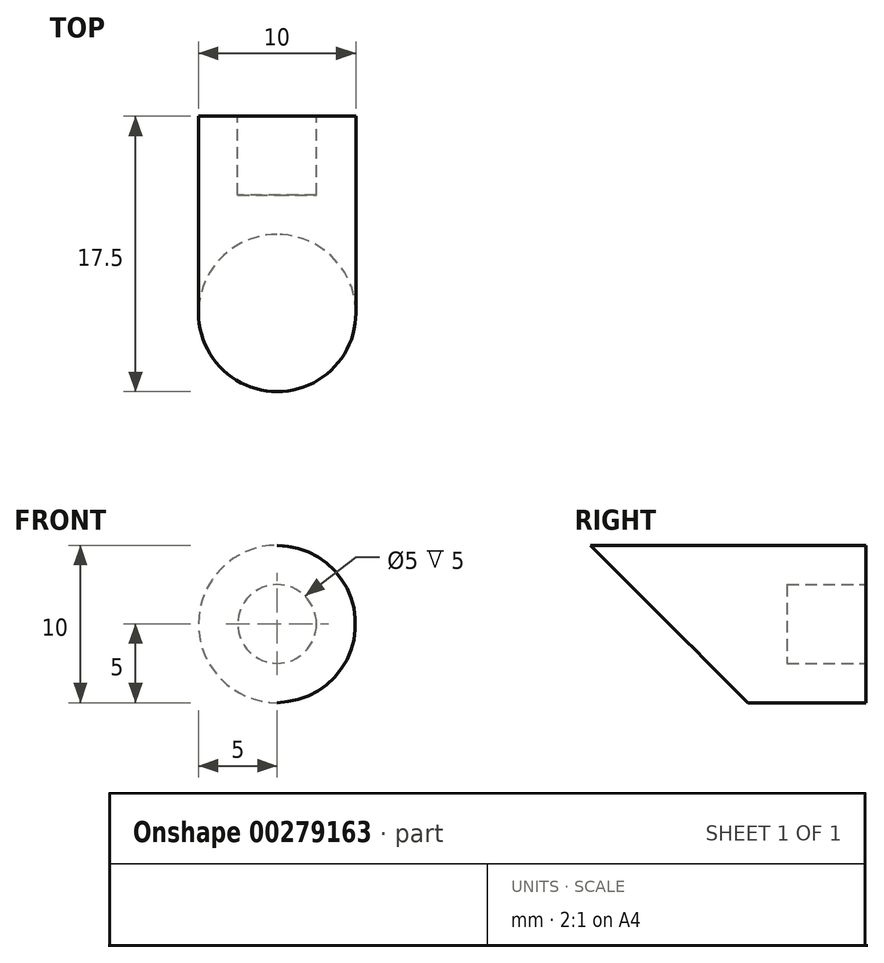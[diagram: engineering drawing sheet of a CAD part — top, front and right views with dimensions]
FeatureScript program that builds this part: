
annotation { "Feature Type Name" : "Feature", "Feature Type Description" : "" }
export const myFeature = defineFeature(function(context is Context, id is Id, definition is map)
    precondition{}
    {
        {
            var Q0;
            Q0=qCreatedBy(makeId("Front.planeOp"),FACE);
            var sketch = newSketch(context, id + "F0", { "sketchPlane" : qUnion([Q0])});
            skCircle(sketch, "E0", {"center": v(0, 0) * mm, "radius": 5 * mm});
            skLineSegment(sketch, "E1", {"start": v(0, 0) * mm, "end": v(5, 0) * mm});
            skSolve(sketch);
        }
        {
            var Q0;
            Q0=makeQuery(id+"F0.imprint","IMPRINT",FACE,{"disambiguationData":[TD([[makeQuery(id+"F0.imprint","IMPRINT",EDGE,{"derivedFrom":sQuery(id+"F0.wireOp",EDGE,"E0")}),1.0]])]});
            extrude(context, id + "F1", {"entities" : qUnion([Q0]), "endBound" : BoundingType.SYMMETRIC, "oppositeDirection" : true, "depth" : 25 * mm});
        }
        {
            var Q0;
            Q0=sQuery(id+"F0.wireOp",EDGE,"E1");
            cPlane(context, id + "F2", {"entities" : qUnion([Q0]), "cplaneType" : CPlaneType.LINE_ANGLE, "offset" : 25 * mm, "angle" : 45 * degree, "width" : 150 * mm, "height" : 150 * mm});
        }
        {
            var Q0;
            Q0=qCreatedBy(id+"F2.planeOp",FACE);
            var sketch = newSketch(context, id + "F3", { "sketchPlane" : qUnion([Q0])});
            skLineSegment(sketch, "E2.bottom", {"start": v(-25, -25) * mm, "end": v(25, -25) * mm});
            skLineSegment(sketch, "E2.top", {"start": v(-25, 25) * mm, "end": v(25, 25) * mm});
            skLineSegment(sketch, "E2.left", {"start": v(-25, -25) * mm, "end": v(-25, 25) * mm});
            skLineSegment(sketch, "E2.right", {"start": v(25, -25) * mm, "end": v(25, 25) * mm});
            skPoint(sketch, "E2.middle", {"position": v(0, 0) * mm});
            skSolve(sketch);
        }
        {
            var Q0;
            Q0=makeQuery(id+"F3.imprint","IMPRINT",FACE,{"disambiguationData":[TD([[makeQuery(id+"F3.imprint","IMPRINT",EDGE,{"derivedFrom":sQuery(id+"F3.wireOp",EDGE,"E2.bottom")}),1.0]])]});
            extrude(context, id + "F4", {"entities" : qUnion([Q0]), "operationType" : NewBodyOperationType.REMOVE, "oppositeDirection" : true, "depth" : 25 * mm});
        }
        {
            var Q0;
            Q0=makeQuery(id+"F1.opExtrude","CAP_FACE",FACE,{"disambiguationData":[OSD([sQuery(id+"F0.wireOp",EDGE,"E0")])],"isStart":false});
            var sketch = newSketch(context, id + "F5", { "sketchPlane" : qUnion([Q0])});
            skCircle(sketch, "E3", {"center": v(0, 0) * mm, "radius": 2.5 * mm});
            skSolve(sketch);
        }
        {
            var Q0;
            Q0=makeQuery(id+"F5.imprint","IMPRINT",FACE,{"disambiguationData":[TD([[makeQuery(id+"F5.imprint","IMPRINT",EDGE,{"derivedFrom":sQuery(id+"F5.wireOp",EDGE,"E3")}),1.0]])]});
            extrude(context, id + "F6", {"entities" : qUnion([Q0]), "operationType" : NewBodyOperationType.REMOVE, "oppositeDirection" : true, "depth" : 5 * mm});
        }
    });
